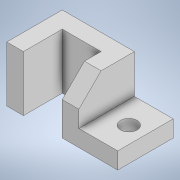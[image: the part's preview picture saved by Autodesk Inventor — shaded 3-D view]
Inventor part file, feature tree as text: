
AUTODESK INVENTOR PART (.ipt)
format: ipt  version: 2020 (Build 240168000, 168)  size: 130,048 bytes
history: native  units: in
note: dims shown in document units (in); Inventor stores cm internally (conversion verified against a paired STEP export)
features: extrude x4, sketch x3, other x1
ambient origin geometry x8: Origin, YZ Plane, XZ Plane, XY Plane, X Axis, Y Axis, Z Axis, Center Point
bodies: Solid1 (feature_tree)
feature tree (8):
  extrude  "baseExtrude"  Depth=2.5in
  extrude  "Extrusion2"  Depth=0.75in
  extrude  "Extrusion3"  Depth=2.5in
  extrude  "Extrusion4"  Depth=2.5in
  other  "baseSketch"
  sketch  "Sketch2"  dims[d0=2.5in d1=2.5in]
  sketch  "Sketch3"  dims[d2=0.75in d3=0.75in]
  sketch  "Sketch4"  dims[d4=2.5in d5=0.0in d6=2.5in d7=2.5in d8=0.75in d9=0.75in d10=2.5in d11=0.0in d12=0.75in d13=0.75in d14=1.25in d15=0.0in d16=0.0in d17=1.0in d18=45.0deg d19=2.5in d20=0.0in]
